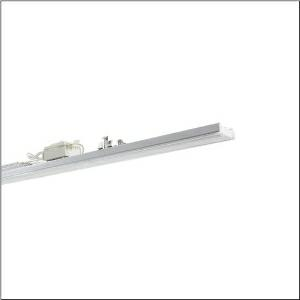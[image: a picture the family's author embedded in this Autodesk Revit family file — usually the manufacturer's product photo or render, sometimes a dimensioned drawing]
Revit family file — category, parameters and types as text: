
# Revit family: licross_r__11_recessed_ho_51te18dv4l5m_9c95
name_source: partatom
category: Lighting Fixtures
units: mm (PartAtom-declared; Revit-internal decimal feet)

## family parameters
Cut with Voids When Loaded = No
Host = Face
Light Source = No
Part Type = Normal
Room Calculation Point = No
Round Connector Dimension = Use Diameter
Shared = No

## types (1)
- --- (1 x LED, 20760 lm, 111.8 W, 4000K)
    Apparent Load = 112 VA
    CIE Flux Codes = 78 94 99 100 100
    Color Rendering = 80
    Color Temperature = 4000K
    Default Elevation = 1800 mm
    Description = Licross® 11 Recessed HO, luminaire insert, of sheet steel, galvanised, coil coated, white, length: 2.250mm, width: 66mm, height: 67mm, LED rated luminous flux: 20.760lm, light colour: 840, control gear: DALI 2, with plug, 5-pole, with phase selection, mains connection: 220..240V, AC, 50/60Hz, rated input power: 112W, halogen-free wiring, primary light control with lens, of plastic, primary optical cover: cover, of PMMA, light emission: direct distribution, primary light characteristic: symmetric, protection rating (complete): IP54, insulation class (complete): insulation class I (protective earthing), certification: CE, ENEC, VDE, UKCA, protection symbol: D if used in an environment with non-conductive dust loads with corresponding accessories, impact resistance: IK06, permissible ambient temperature for indoor applications: -40..+45°C, corresponds to IFS (International Featured Standards) requirements for safety and quality in the food industry, reducing of maximum allowable ambient temperature of 5°C with ceiling mounting, LABS conformity tested according to VDMA 24364:2018-05, packaging unit: 1 piece
    Height = 58 mm
    Lamp = 1 x LED
    Lamp Light Flux = 20760 lm
    Lamp Power = 111.8 W
    Lamp count = 1
    Length = 2250 mm
    Luminous efficacy = 186 lm/W
    Manufacturer = Siteco
    ModVariant = No
    Model = 51TE18DV4L5M
    Mounting Place = Ceiling
    Mounting Type = Pendant
    Number of Poles = 1
    OnlyDefault = Yes
    Power Factor = 1
    Product Name = Licross® 11 Recessed HO
    Product group = luminaire insert
    ProductGroupID = 902
    Protection Class = Protection class I
    Protection Degree = IP 54
    RLX_Detail_Level = 1
    RLX_Emergency_Light_Flux = 0 lm
    RLX_Emergency_Type = 0
    RLX_Emergency_Type_DB = No
    RlxData = <blob elided: 29477 chars, md5=8a2c8fea>
    Socket = socket
    Standby Power = 0 W
    System Light Flux = 20760 lm
    System Power = 112 W
    Type Comments = factory setting: luminous flux: 100 % | dim-lin: 254 | 520 mA
    Type Image = l_1296930.jpg
    URL = http://relux.com
    VarID = @adj_099320
    Voltage = 0 V
    Weight = 0.00 kg
    Width = 66 mm

## geometry (parser evidence)
native form markers: Blend x4, Sweep x8
no freeform markers — native parametric forms only
